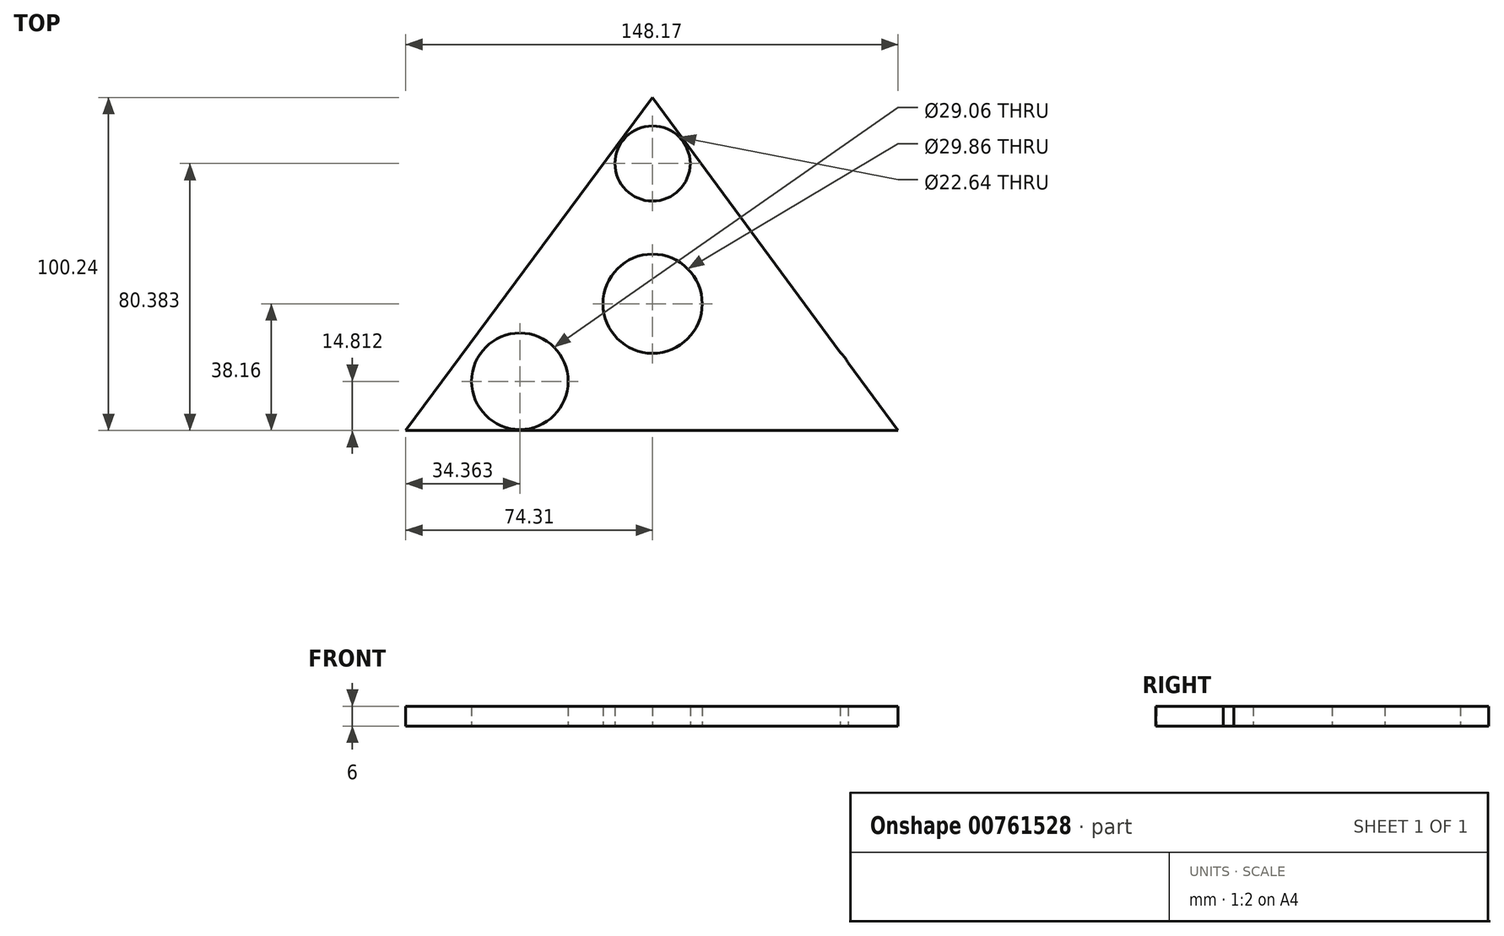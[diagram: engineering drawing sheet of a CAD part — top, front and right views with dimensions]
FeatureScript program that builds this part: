
annotation { "Feature Type Name" : "Feature", "Feature Type Description" : "" }
export const myFeature = defineFeature(function(context is Context, id is Id, definition is map)
    precondition{}
    {
        {
            var Q0;
            Q0=qCreatedBy(makeId("Top.planeOp"),FACE);
            var sketch = newSketch(context, id + "F0", { "sketchPlane" : qUnion([Q0])});
            skLineSegment(sketch, "E0", {"start": v(-49.7, 0) * mm, "end": v(39, 0) * mm});
            skLineSegment(sketch, "E1", {"start": v(0, 62.08) * mm, "end": v(-74.3, -38.16) * mm});
            skLineSegment(sketch, "E2", {"start": v(-74.3, -38.16) * mm, "end": v(73.86, -38.16) * mm});
            skLineSegment(sketch, "E3", {"start": v(73.86, -38.16) * mm, "end": v(0, 62.08) * mm});
            skCircle(sketch, "E4", {"center": v(0, 0) * mm, "radius": 14.93 * mm});
            skCircle(sketch, "E5", {"center": v(0, 42.22) * mm, "radius": 11.32 * mm});
            skCircle(sketch, "E6", {"center": v(-39.95, -23.35) * mm, "radius": 14.53 * mm});
            skCircle(sketch, "E7", {"center": v(46.75, -24.3) * mm, "radius": 13.74 * mm});
            skSolve(sketch);
        }
        {
            var Q0;
            Q0 = qSketchRegion(id + "F0", true);
            extrude(context, id + "F1", {"entities" : qUnion([Q0]), "depth" : 6 * mm, "offsetDistance" : 25 * mm});
        }
        {
            var Q0;
            Q0=sQuery(id+"F0.wireOp",EDGE,"E7");
            extrude(context, id + "F2", {"bodyType" : ToolBodyType.SURFACE, "surfaceEntities" : qUnion([Q0]), "depth" : 6 * mm, "offsetDistance" : 25 * mm});
        }
    });
